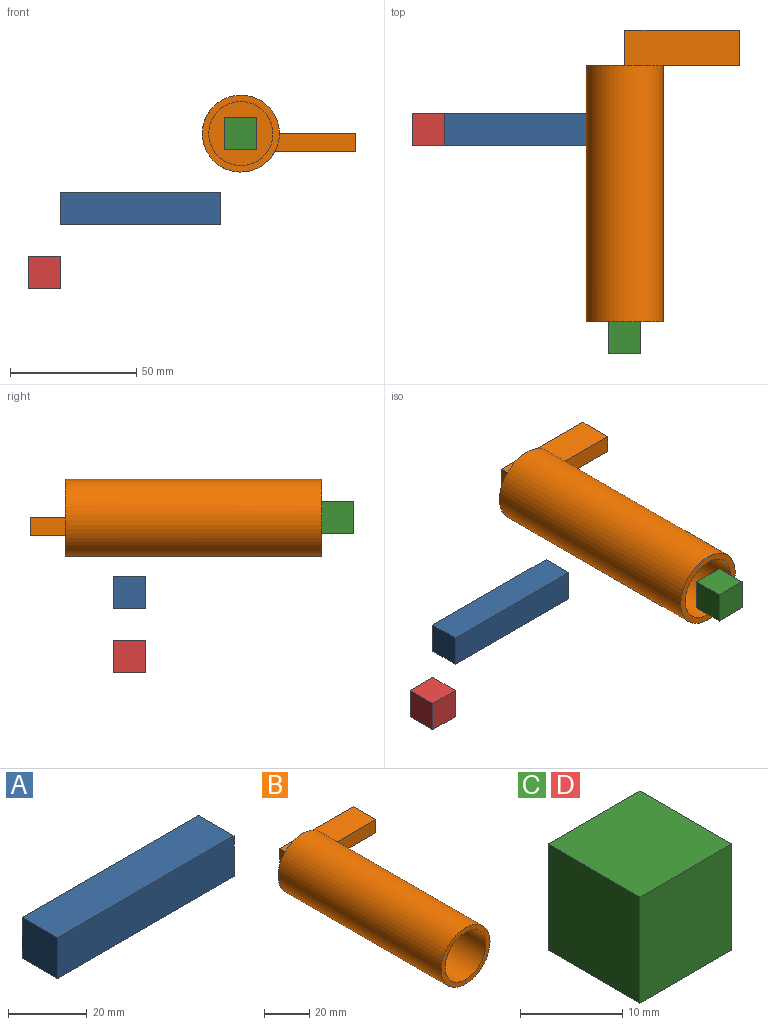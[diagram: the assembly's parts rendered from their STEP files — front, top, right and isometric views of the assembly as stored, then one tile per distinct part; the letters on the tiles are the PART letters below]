
ASSEMBLY  parts=4 mates=2
PART A: 6 faces, bbox 63.5x12.7x12.7 mm
  f0: plane 63.5x12.7mm, normal (0,0,-1), area 806.5mm2, adj f1,f3,f4,f5
  f1: plane 12.7x12.7mm, normal (1,0,0), area 161.3mm2, adj f0,f2,f4,f5
  f2: plane 63.5x12.7mm, normal (0,0,1), area 806.5mm2, adj f1,f3,f4,f5
  f3: plane 12.7x12.7mm, normal (-1,0,0), area 161.3mm2, adj f0,f2,f4,f5
  f4: plane 63.5x12.7mm, normal (0,-1,0), area 806.5mm2, adj f0,f1,f2,f3
  f5: plane 63.5x12.7mm, normal (0,1,0), area 806.5mm2, adj f0,f1,f2,f3
PART B: 11 faces, bbox 60.8x115.6x30.5 mm
  f0: cylinder r=15.24mm len=101.6mm, axis (0,1,0), area 9728.8mm2, adj f1,f2,f9
  f1: plane 30.48x30.48mm, normal (0,-1,0), area 223mm2, adj f0,f3
  f2: plane 30.48x30.48mm, normal (0,1,0), area 624.7mm2, adj f0,f5,f6,f7
  f3: cylinder r=12.7mm len=99.06mm, axis (0,1,0), area 7904.6mm2, adj f1,f4
  f4: plane 25.4x25.4mm, normal (0,-1,0), area 506.7mm2, adj f3
  f5: plane 45.53x14mm, normal (0,0,-1), area 637.3mm2, adj f2,f6,f8,f9,f10
  f6: plane 14x7.16mm, normal (-1,0,0), area 100.2mm2, adj f2,f5,f7,f10
  f7: plane 45.53x14mm, normal (0,0,1), area 637.3mm2, adj f2,f6,f8,f9,f10
  f8: plane 14x7.16mm, normal (1,0,0), area 100.2mm2, adj f5,f7,f9,f10
  f9: plane 32.08x7.16mm, normal (0,-1,0), area 221.1mm2, adj f0,f5,f7,f8
  f10: plane 45.53x7.16mm, normal (0,1,0), area 326.1mm2, adj f5,f6,f7,f8
PART C: 6 faces, bbox 12.7x12.7x12.7 mm
  f0: plane 12.7x12.7mm, normal (0,0,-1), area 161.3mm2, adj f1,f3,f4,f5
  f1: plane 12.7x12.7mm, normal (1,0,0), area 161.3mm2, adj f0,f2,f4,f5
  f2: plane 12.7x12.7mm, normal (0,0,1), area 161.3mm2, adj f1,f3,f4,f5
  f3: plane 12.7x12.7mm, normal (-1,0,0), area 161.3mm2, adj f0,f2,f4,f5
  f4: plane 12.7x12.7mm, normal (0,-1,0), area 161.3mm2, adj f0,f1,f2,f3
  f5: plane 12.7x12.7mm, normal (0,1,0), area 161.3mm2, adj f0,f1,f2,f3
PART D: same geometry as C
PLACE A t=(2.08,-7.06,24.45)mm
PLACE B t=(38.54,11.85,10.58)mm
PLACE C t=(38.54,-89.75,-18)mm
PLACE D t=(-39.33,-7.06,-73.14)mm
MATE planar C.f5 <-> B.f0  axis (0,1,0) through (38.54,-89.75,10.58)mm
MATE fastened D.f1 <-> A.f3  axis (1,0,0) through (-32.98,-13.41,-44.56)mm
